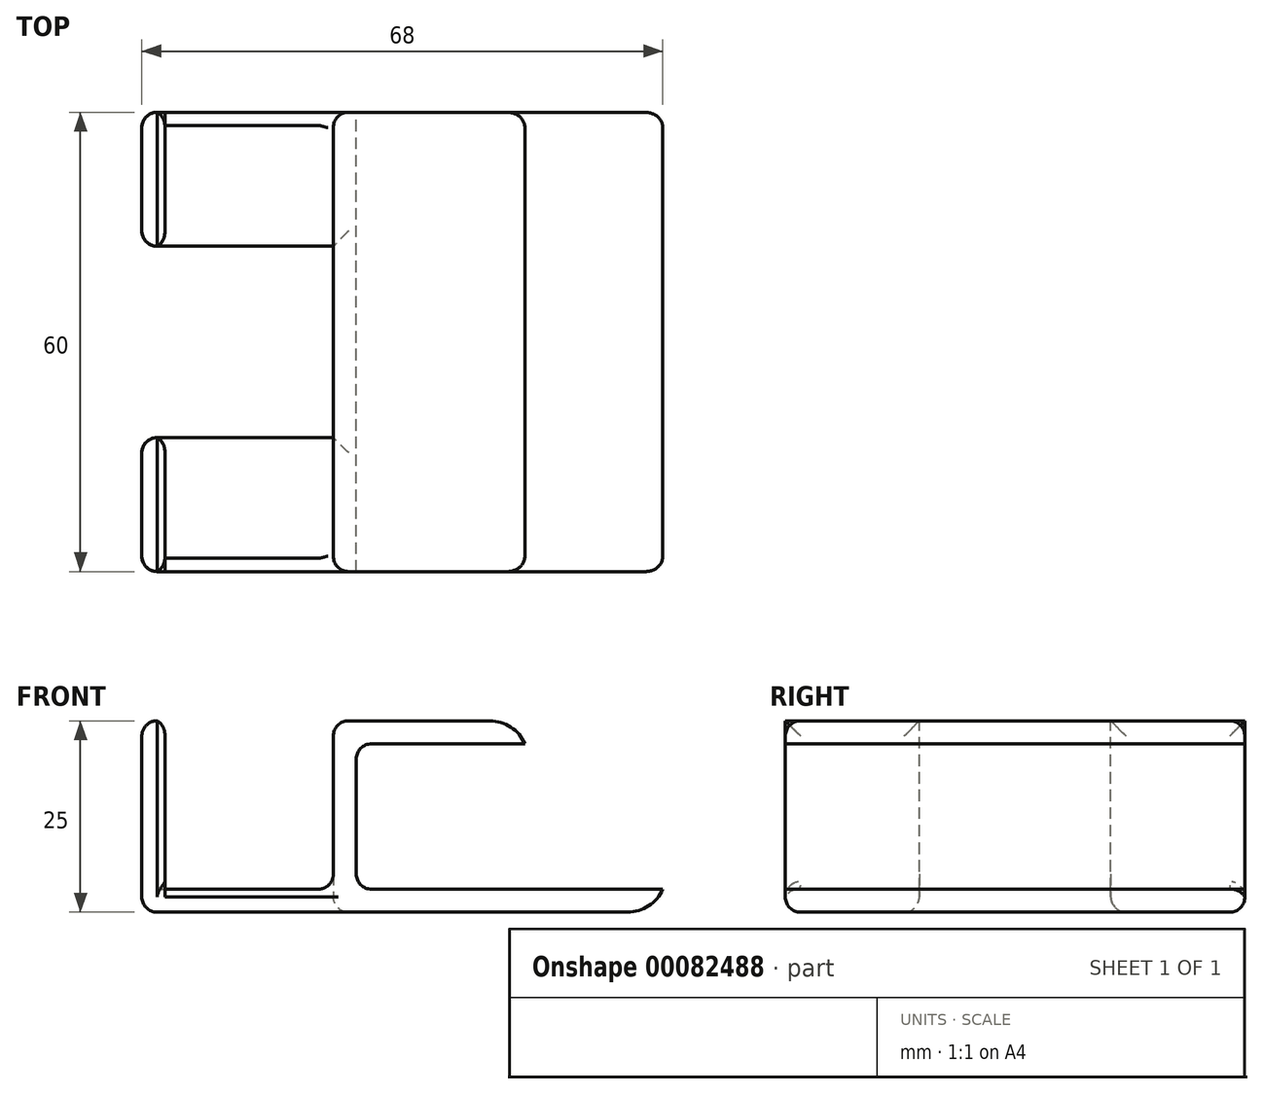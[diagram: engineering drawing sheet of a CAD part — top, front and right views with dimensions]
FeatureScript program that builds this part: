
annotation { "Feature Type Name" : "Feature", "Feature Type Description" : "" }
export const myFeature = defineFeature(function(context is Context, id is Id, definition is map)
    precondition{}
    {
        {
            assignVariable(context, id + "F0", {"name" : "totalWidth", "anyValue" : 60});
        }
        {
            var Q0;
            Q0=qCreatedBy(makeId("Front.planeOp"),FACE);
            var sketch = newSketch(context, id + "F1", { "sketchPlane" : qUnion([Q0])});
            skLineSegment(sketch, "E0.bottom", {"start": v(-34, 1.5) * mm, "end": v(34, 1.5) * mm});
            skLineSegment(sketch, "E0.top", {"start": v(-34, -1.5) * mm, "end": v(34, -1.5) * mm});
            skLineSegment(sketch, "E0.left", {"start": v(-34, 1.5) * mm, "end": v(-34, -1.5) * mm});
            skLineSegment(sketch, "E0.right", {"start": v(34, 1.5) * mm, "end": v(34, -1.5) * mm});
            skPoint(sketch, "E0.middle", {"position": v(0, 0) * mm});
            skLineSegment(sketch, "E1.bottom", {"start": v(-34, 1.5) * mm, "end": v(-31, 1.5) * mm});
            skLineSegment(sketch, "E1.top", {"start": v(-34, 23.5) * mm, "end": v(-31, 23.5) * mm});
            skLineSegment(sketch, "E1.left", {"start": v(-34, 1.5) * mm, "end": v(-34, 23.5) * mm});
            skLineSegment(sketch, "E1.right", {"start": v(-31, 1.5) * mm, "end": v(-31, 23.5) * mm});
            skLineSegment(sketch, "E2.bottom", {"start": v(-9, 1.5) * mm, "end": v(-6, 1.5) * mm});
            skLineSegment(sketch, "E2.top", {"start": v(-9, 23.5) * mm, "end": v(-6, 23.5) * mm});
            skLineSegment(sketch, "E2.left", {"start": v(-6, 1.5) * mm, "end": v(-6, 23.5) * mm});
            skLineSegment(sketch, "E2.right", {"start": v(-9, 1.5) * mm, "end": v(-9, 23.5) * mm});
            skLineSegment(sketch, "E3.bottom", {"start": v(-6, 23.5) * mm, "end": v(16, 23.5) * mm});
            skLineSegment(sketch, "E3.top", {"start": v(-6, 20.5) * mm, "end": v(16, 20.5) * mm});
            skLineSegment(sketch, "E3.left", {"start": v(-6, 23.5) * mm, "end": v(-6, 20.5) * mm});
            skLineSegment(sketch, "E3.right", {"start": v(16, 23.5) * mm, "end": v(16, 20.5) * mm});
            skSolve(sketch);
        }
        {
            var Q0;
            Q0 = qSketchRegion(id + "F1", true);
            extrude(context, id + "F2", {"entities" : qUnion([Q0]), "endBound" : BoundingType.SYMMETRIC, "depth" : (getVariable(context, 'totalWidth')) * mm});
        }
        {
            var Q0;
            {var subQ0=sQuery(id+"F1.wireOp",EDGE,"E0.bottom");Q0=makeQuery(id+"F2.opExtrude","SWEPT_FACE",FACE,{"disambiguationData":[OSD([subQ0]),TDD([makeQuery(id+"F1.imprint","IMPRINT",EDGE,{"disambiguationData":[TD([[makeQuery(id+"F1.imprint","INTERSECT",VERTEX,{"derivedFrom":[subQ0,sQuery(id+"F1.wireOp",EDGE,"E1.bottom"),sQuery(id+"F1.wireOp",EDGE,"E1.right")]}),-1.0]])],"derivedFrom":subQ0})])]});}
            var sketch = newSketch(context, id + "F3", { "sketchPlane" : qUnion([Q0])});
            skLineSegment(sketch, "E4.bottom", {"start": v(-9, 12.5) * mm, "end": v(-45.95, 12.5) * mm});
            skLineSegment(sketch, "E4.top", {"start": v(-9, -12.5) * mm, "end": v(-45.95, -12.5) * mm});
            skLineSegment(sketch, "E4.left", {"start": v(-9, 12.5) * mm, "end": v(-9, -12.5) * mm});
            skLineSegment(sketch, "E4.right", {"start": v(-45.95, 12.5) * mm, "end": v(-45.95, -12.5) * mm});
            skPoint(sketch, "E5", {"position": v(-9, 0) * mm});
            skSolve(sketch);
        }
        {
            var Q0;
            {var subQ0=sQuery(id+"F3.wireOp",EDGE,"E4.right");Q0=makeQuery(id+"F3.imprint","IMPRINT",FACE,{"disambiguationData":[TD([[makeQuery(id+"F3.imprint","IMPRINT",EDGE,{"derivedFrom":subQ0}),1.0]])]});}
            var Q1;
            {var subQ0=sQuery(id+"F3.wireOp",EDGE,"E4.left");Q1=makeQuery(id+"F3.imprint","IMPRINT",FACE,{"disambiguationData":[TD([[makeQuery(id+"F3.imprint","IMPRINT",EDGE,{"derivedFrom":subQ0}),1.0]])]});}
            extrude(context, id + "F4", {"entities" : qUnion([Q0, Q1]), "operationType" : NewBodyOperationType.REMOVE, "endBound" : BoundingType.SYMMETRIC, "depth" : 130.8 * mm});
        }
        {
            var Q0;
            Q0=makeQuery(id+"F2.opExtrude","SWEPT_EDGE",EDGE,{"disambiguationData":[OSD([sQuery(id+"F1.wireOp",EDGE,"E3.bottom"),sQuery(id+"F1.wireOp",EDGE,"E3.right")])]});
            var Q1;
            Q1=makeQuery(id+"F2.opExtrude","SWEPT_EDGE",EDGE,{"disambiguationData":[OSD([sQuery(id+"F1.wireOp",EDGE,"E0.top"),sQuery(id+"F1.wireOp",EDGE,"E0.right")])]});
            fillet(context, id + "F5", {"entities" : qUnion([Q0, Q1]), "radius" : 5 * mm, "tangentPropagation" : true, "allowEdgeOverflow" : false});
        }
        {
            var Q0;
            {var subQ0=sQuery(id+"F1.wireOp",EDGE,"E2.right");var subQ2=sQuery(id+"F1.wireOp",EDGE,"E0.bottom");var subQ3=sQuery(id+"F1.wireOp",EDGE,"E2.bottom");Q0=makeQuery(id+"F4.boolean.opBoolean","SPLIT",EDGE,{"disambiguationData":[TD([makeQuery(id+"F4.opExtrude","SWEPT_FACE",FACE,{"disambiguationData":[OSD([sQuery(id+"F3.wireOp",EDGE,"E4.top")])]})])],"derivedFrom":makeQuery(id+"F2.opExtrude","SWEPT_EDGE",EDGE,{"disambiguationData":[OSD([subQ2,subQ3,subQ0])]})});}
            var Q1;
            {var subQ0=sQuery(id+"F1.wireOp",EDGE,"E2.right");var subQ2=sQuery(id+"F1.wireOp",EDGE,"E0.bottom");var subQ3=sQuery(id+"F1.wireOp",EDGE,"E2.bottom");Q1=makeQuery(id+"F4.boolean.opBoolean","SPLIT",EDGE,{"disambiguationData":[TD([makeQuery(id+"F4.opExtrude","SWEPT_FACE",FACE,{"disambiguationData":[OSD([sQuery(id+"F3.wireOp",EDGE,"E4.bottom")])]})])],"derivedFrom":makeQuery(id+"F2.opExtrude","SWEPT_EDGE",EDGE,{"disambiguationData":[OSD([subQ2,subQ3,subQ0])]})});}
            fillet(context, id + "F6", {"entities" : qUnion([Q0, Q1]), "radius" : 2 * mm, "allowEdgeOverflow" : false});
        }
        {
            var Q0;
            Q0=makeQuery(id+"F2.opExtrude","SWEPT_EDGE",EDGE,{"disambiguationData":[OSD([sQuery(id+"F1.wireOp",EDGE,"E2.top"),sQuery(id+"F1.wireOp",EDGE,"E2.right")])]});
            fillet(context, id + "F7", {"entities" : qUnion([Q0]), "radius" : 2 * mm, "tangentPropagation" : true, "allowEdgeOverflow" : false});
        }
        {
            var Q0;
            Q0=makeQuery(id+"F2.opExtrude","CAP_EDGE",EDGE,{"disambiguationData":[OSD([sQuery(id+"F1.wireOp",EDGE,"E2.top"),sQuery(id+"F1.wireOp",EDGE,"E3.bottom")])],"isStart":false});
            var Q1;
            Q1=makeQuery(id+"F2.opExtrude","CAP_EDGE",EDGE,{"disambiguationData":[OSD([sQuery(id+"F1.wireOp",EDGE,"E2.top"),sQuery(id+"F1.wireOp",EDGE,"E3.bottom")])],"isStart":true});
            var Q2;
            Q2=makeQuery(id+"F2.opExtrude","CAP_EDGE",EDGE,{"disambiguationData":[OSD([sQuery(id+"F1.wireOp",EDGE,"E0.top")])],"isStart":true});
            var Q3;
            Q3=makeQuery(id+"F2.opExtrude","CAP_EDGE",EDGE,{"disambiguationData":[OSD([sQuery(id+"F1.wireOp",EDGE,"E0.top")])],"isStart":false});
            var Q4;
            {var subQ1=sQuery(id+"F1.wireOp",EDGE,"E0.left");var subQ2=sQuery(id+"F1.wireOp",EDGE,"E0.top");Q4=makeQuery(id+"F4.boolean.opBoolean","SPLIT",EDGE,{"disambiguationData":[TD([makeQuery(id+"F4.opExtrude","SWEPT_FACE",FACE,{"disambiguationData":[OSD([sQuery(id+"F3.wireOp",EDGE,"E4.bottom")])]})])],"derivedFrom":makeQuery(id+"F2.opExtrude","SWEPT_EDGE",EDGE,{"disambiguationData":[OSD([subQ2,subQ1])]})});}
            var Q5;
            {var subQ1=sQuery(id+"F1.wireOp",EDGE,"E0.left");var subQ2=sQuery(id+"F1.wireOp",EDGE,"E0.top");Q5=makeQuery(id+"F4.boolean.opBoolean","SPLIT",EDGE,{"disambiguationData":[TD([makeQuery(id+"F4.opExtrude","SWEPT_FACE",FACE,{"disambiguationData":[OSD([sQuery(id+"F3.wireOp",EDGE,"E4.top")])]})])],"derivedFrom":makeQuery(id+"F2.opExtrude","SWEPT_EDGE",EDGE,{"disambiguationData":[OSD([subQ2,subQ1])]})});}
            var Q6;
            Q6=makeQuery(id+"F4.boolean.opBoolean","INTERSECT",EDGE,{"derivedFrom":[makeQuery(id+"F2.opExtrude","SWEPT_FACE",FACE,{"disambiguationData":[OSD([sQuery(id+"F1.wireOp",EDGE,"E0.top")])]}),makeQuery(id+"F4.opExtrude","SWEPT_FACE",FACE,{"disambiguationData":[OSD([sQuery(id+"F3.wireOp",EDGE,"E4.top")])]})]});
            var Q7;
            Q7=makeQuery(id+"F4.boolean.opBoolean","INTERSECT",EDGE,{"derivedFrom":[makeQuery(id+"F2.opExtrude","SWEPT_FACE",FACE,{"disambiguationData":[OSD([sQuery(id+"F1.wireOp",EDGE,"E0.top")])]}),makeQuery(id+"F4.opExtrude","SWEPT_FACE",FACE,{"disambiguationData":[OSD([sQuery(id+"F3.wireOp",EDGE,"E4.bottom")])]})]});
            var Q8;
            Q8=makeQuery(id+"F4.boolean.opBoolean","INTERSECT",EDGE,{"derivedFrom":[makeQuery(id+"F2.opExtrude","SWEPT_FACE",FACE,{"disambiguationData":[OSD([sQuery(id+"F1.wireOp",EDGE,"E0.top")])]}),makeQuery(id+"F4.opExtrude","SWEPT_FACE",FACE,{"disambiguationData":[OSD([sQuery(id+"F3.wireOp",EDGE,"E4.left")])]})]});
            fillet(context, id + "F8", {"entities" : qUnion([Q0, Q1, Q2, Q3, Q4, Q5, Q6, Q7, Q8]), "radius" : 2 * mm, "tangentPropagation" : true, "allowEdgeOverflow" : false});
        }
        {
            var Q0;
            {var subQ0=sQuery(id+"F1.wireOp",EDGE,"E1.left");var subQ1=sQuery(id+"F1.wireOp",EDGE,"E1.top");Q0=makeQuery(id+"F4.boolean.opBoolean","SPLIT",EDGE,{"disambiguationData":[TD([makeQuery(id+"F4.opExtrude","SWEPT_FACE",FACE,{"disambiguationData":[OSD([sQuery(id+"F3.wireOp",EDGE,"E4.bottom")])]})])],"derivedFrom":makeQuery(id+"F2.opExtrude","SWEPT_EDGE",EDGE,{"disambiguationData":[OSD([subQ1,subQ0])]})});}
            var Q1;
            {var subQ0=sQuery(id+"F1.wireOp",EDGE,"E1.left");var subQ1=sQuery(id+"F1.wireOp",EDGE,"E1.top");Q1=makeQuery(id+"F4.boolean.opBoolean","SPLIT",EDGE,{"disambiguationData":[TD([makeQuery(id+"F4.opExtrude","SWEPT_FACE",FACE,{"disambiguationData":[OSD([sQuery(id+"F3.wireOp",EDGE,"E4.top")])]})])],"derivedFrom":makeQuery(id+"F2.opExtrude","SWEPT_EDGE",EDGE,{"disambiguationData":[OSD([subQ1,subQ0])]})});}
            var Q2;
            Q2=makeQuery(id+"F4.boolean.opBoolean","INTERSECT",EDGE,{"derivedFrom":[makeQuery(id+"F2.opExtrude","SWEPT_FACE",FACE,{"disambiguationData":[OSD([sQuery(id+"F1.wireOp",EDGE,"E0.left"),sQuery(id+"F1.wireOp",EDGE,"E1.left")])]}),makeQuery(id+"F4.opExtrude","SWEPT_FACE",FACE,{"disambiguationData":[OSD([sQuery(id+"F3.wireOp",EDGE,"E4.top")])]})]});
            var Q3;
            Q3=makeQuery(id+"F2.opExtrude","CAP_EDGE",EDGE,{"disambiguationData":[OSD([sQuery(id+"F1.wireOp",EDGE,"E0.left"),sQuery(id+"F1.wireOp",EDGE,"E1.left")])],"isStart":false});
            var Q4;
            Q4=makeQuery(id+"F2.opExtrude","CAP_EDGE",EDGE,{"disambiguationData":[OSD([sQuery(id+"F1.wireOp",EDGE,"E0.left"),sQuery(id+"F1.wireOp",EDGE,"E1.left")])],"isStart":true});
            var Q5;
            Q5=makeQuery(id+"F4.boolean.opBoolean","INTERSECT",EDGE,{"derivedFrom":[makeQuery(id+"F2.opExtrude","SWEPT_FACE",FACE,{"disambiguationData":[OSD([sQuery(id+"F1.wireOp",EDGE,"E0.left"),sQuery(id+"F1.wireOp",EDGE,"E1.left")])]}),makeQuery(id+"F4.opExtrude","SWEPT_FACE",FACE,{"disambiguationData":[OSD([sQuery(id+"F3.wireOp",EDGE,"E4.bottom")])]})]});
            fillet(context, id + "F9", {"entities" : qUnion([Q0, Q1, Q2, Q3, Q4, Q5]), "radius" : 2 * mm, "tangentPropagation" : true, "allowEdgeOverflow" : false});
        }
        {
            var Q0;
            {var subQ0=sQuery(id+"F1.wireOp",EDGE,"E1.right");var subQ1=sQuery(id+"F1.wireOp",EDGE,"E1.top");Q0=makeQuery(id+"F4.boolean.opBoolean","SPLIT",EDGE,{"disambiguationData":[TD([makeQuery(id+"F4.opExtrude","SWEPT_FACE",FACE,{"disambiguationData":[OSD([sQuery(id+"F3.wireOp",EDGE,"E4.bottom")])]})])],"derivedFrom":makeQuery(id+"F2.opExtrude","SWEPT_EDGE",EDGE,{"disambiguationData":[OSD([subQ1,subQ0])]})});}
            var Q1;
            {var subQ0=sQuery(id+"F1.wireOp",EDGE,"E1.right");var subQ1=sQuery(id+"F1.wireOp",EDGE,"E1.top");Q1=makeQuery(id+"F4.boolean.opBoolean","SPLIT",EDGE,{"disambiguationData":[TD([makeQuery(id+"F4.opExtrude","SWEPT_FACE",FACE,{"disambiguationData":[OSD([sQuery(id+"F3.wireOp",EDGE,"E4.top")])]})])],"derivedFrom":makeQuery(id+"F2.opExtrude","SWEPT_EDGE",EDGE,{"disambiguationData":[OSD([subQ1,subQ0])]})});}
            var Q2;
            Q2=makeQuery(id+"F4.boolean.opBoolean","INTERSECT",EDGE,{"derivedFrom":[makeQuery(id+"F2.opExtrude","SWEPT_FACE",FACE,{"disambiguationData":[OSD([sQuery(id+"F1.wireOp",EDGE,"E1.right")])]}),makeQuery(id+"F4.opExtrude","SWEPT_FACE",FACE,{"disambiguationData":[OSD([sQuery(id+"F3.wireOp",EDGE,"E4.bottom")])]})]});
            var Q3;
            Q3=makeQuery(id+"F2.opExtrude","CAP_EDGE",EDGE,{"disambiguationData":[OSD([sQuery(id+"F1.wireOp",EDGE,"E1.right")])],"isStart":false});
            var Q4;
            Q4=makeQuery(id+"F4.boolean.opBoolean","INTERSECT",EDGE,{"derivedFrom":[makeQuery(id+"F2.opExtrude","SWEPT_FACE",FACE,{"disambiguationData":[OSD([sQuery(id+"F1.wireOp",EDGE,"E1.right")])]}),makeQuery(id+"F4.opExtrude","SWEPT_FACE",FACE,{"disambiguationData":[OSD([sQuery(id+"F3.wireOp",EDGE,"E4.top")])]})]});
            var Q5;
            Q5=makeQuery(id+"F2.opExtrude","CAP_EDGE",EDGE,{"disambiguationData":[OSD([sQuery(id+"F1.wireOp",EDGE,"E1.right")])],"isStart":true});
            fillet(context, id + "F10", {"entities" : qUnion([Q0, Q1, Q2, Q3, Q4, Q5]), "radius" : 2 * mm, "tangentPropagation" : true, "allowEdgeOverflow" : false});
        }
        {
            var Q0;
            Q0=makeQuery(id+"F2.opExtrude","SWEPT_EDGE",EDGE,{"disambiguationData":[OSD([sQuery(id+"F1.wireOp",EDGE,"E0.bottom"),sQuery(id+"F1.wireOp",EDGE,"E2.bottom"),sQuery(id+"F1.wireOp",EDGE,"E2.left")])]});
            var Q1;
            Q1=makeQuery(id+"F2.opExtrude","SWEPT_EDGE",EDGE,{"disambiguationData":[OSD([sQuery(id+"F1.wireOp",EDGE,"E2.left"),sQuery(id+"F1.wireOp",EDGE,"E3.top"),sQuery(id+"F1.wireOp",EDGE,"E3.left")])]});
            fillet(context, id + "F11", {"entities" : qUnion([Q0, Q1]), "radius" : 2 * mm, "tangentPropagation" : true, "allowEdgeOverflow" : false});
        }
    });
